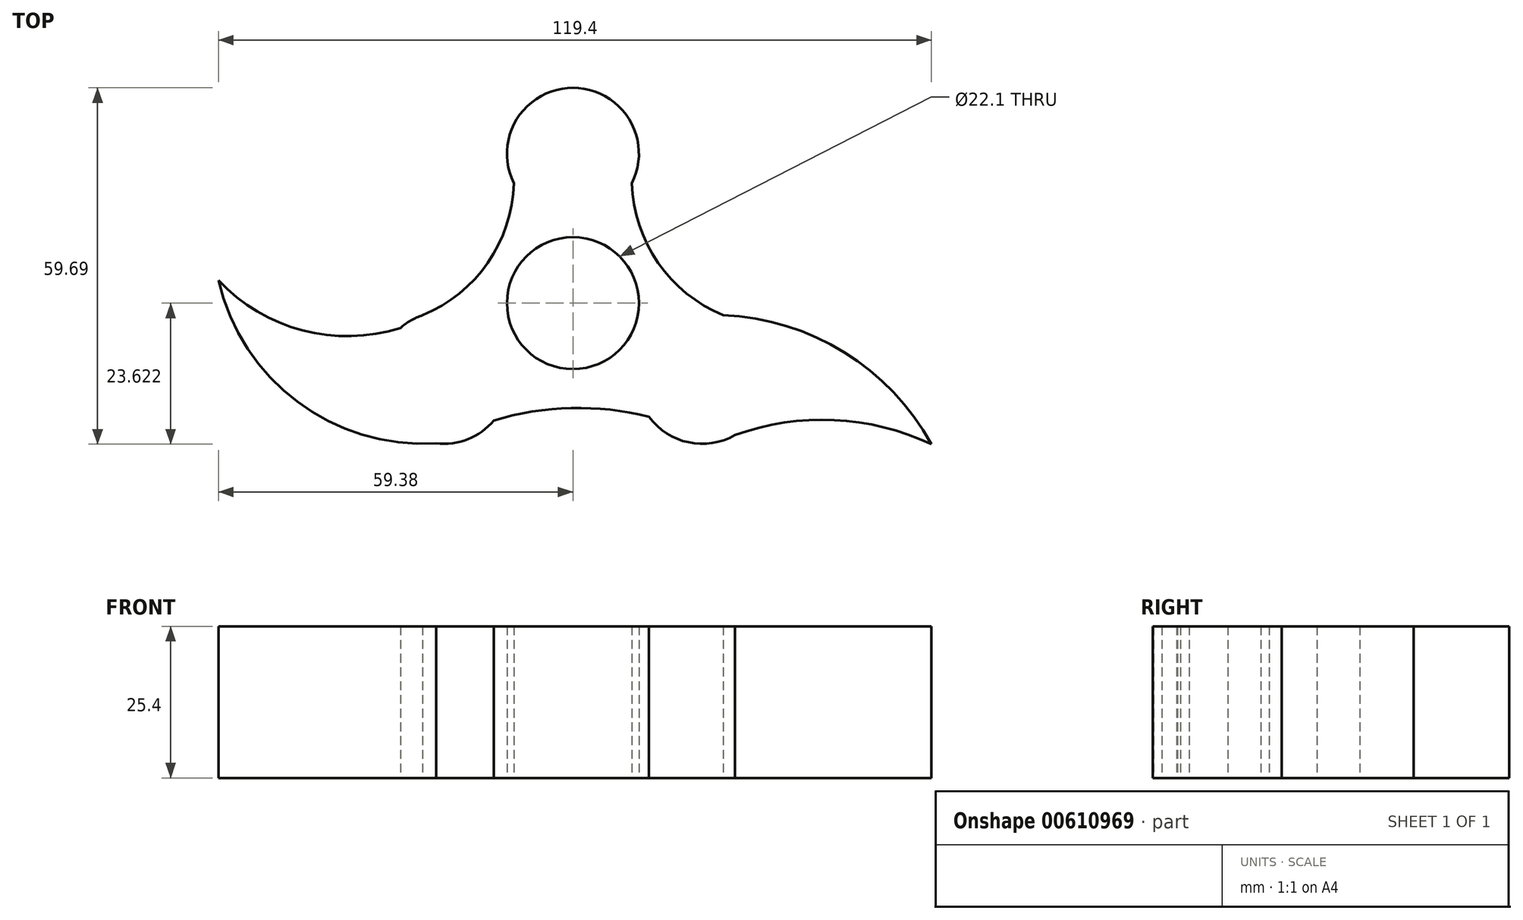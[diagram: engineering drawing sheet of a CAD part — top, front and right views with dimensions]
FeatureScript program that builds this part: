
annotation { "Feature Type Name" : "Feature", "Feature Type Description" : "" }
export const myFeature = defineFeature(function(context is Context, id is Id, definition is map)
    precondition{}
    {
        {
            var Q0;
            Q0=qCreatedBy(makeId("Top.planeOp"),FACE);
            var sketch = newSketch(context, id + "F0", { "sketchPlane" : qUnion([Q0])});
            skCircle(sketch, "E0", {"center": v(0, 48.64) * mm, "radius": 11.05 * mm});
            skCircle(sketch, "E1.1.0", {"center": v(21.67, 11.11) * mm, "radius": 11.05 * mm});
            skCircle(sketch, "E1.2.0", {"center": v(-21.67, 11.11) * mm, "radius": 11.05 * mm});
            skPoint(sketch, "E1.center", {"position": v(0, 23.62) * mm});
            skLineSegment(sketch, "E1.anchor1", {"start": v(0, 23.62) * mm, "end": v(0, 48.64) * mm, "construction": true});
            skLineSegment(sketch, "E1.anchor2", {"start": v(0, 23.62) * mm, "end": v(-21.67, 11.11) * mm, "construction": true});
            skCircle(sketch, "E2", {"center": v(0, 23.62) * mm, "radius": 11.05 * mm});
            skArc(sketch, "E3", {"start": v(-59.38, 27.46) * mm, "mid": v(-45.3, 19.06) * mm, "end": v(-28.9, 19.46) * mm});
            skArc(sketch, "E4", {"start": v(-59.38, 27.46) * mm, "mid": v(-43.9, 5.56) * mm, "end": v(-17.48, 0.89) * mm});
            skArc(sketch, "E5", {"start": v(5.98, 83.33) * mm, "mid": v(-5.24, 71.14) * mm, "end": v(-9.03, 55.01) * mm});
            skArc(sketch, "E6", {"start": v(5.98, 83.33) * mm, "mid": v(6.41, 68.28) * mm, "end": v(10.36, 53.75) * mm});
            skArc(sketch, "E7", {"start": v(60.02, 0) * mm, "mid": v(45.44, 15.4) * mm, "end": v(25.17, 21.6) * mm});
            skArc(sketch, "E8", {"start": v(60.02, 0) * mm, "mid": v(43.74, 4.05) * mm, "end": v(27.16, 1.53) * mm});
            skArc(sketch, "E9", {"start": v(9.88, 43.7) * mm, "mid": v(14.26, 30.39) * mm, "end": v(25.17, 21.6) * mm});
            skArc(sketch, "E10.MirrorCS", {"start": v(-9.88, 43.7) * mm, "mid": v(-14.26, 30.39) * mm, "end": v(-25.17, 21.6) * mm});
            skArc(sketch, "E11", {"start": v(12.74, 4.6) * mm, "mid": v(-0.3, 6.05) * mm, "end": v(-13.24, 3.97) * mm});
            skSolve(sketch);
        }
        {
            var Q0;
            Q0 = qSketchRegion(id + "F0", true);
            extrude(context, id + "F1", {"entities" : qUnion([Q0]), "depth" : 25.4 * mm, "offsetDistance" : 25.4 * mm});
        }
    });
